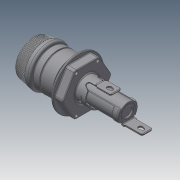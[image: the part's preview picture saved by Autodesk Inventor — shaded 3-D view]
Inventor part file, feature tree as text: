
AUTODESK INVENTOR PART (.ipt)
format: ipt  version: 2020.3 (Build 243373000, 373)  size: 3,708,928 bytes
history: native  units: in
note: dims shown in document units (in); Inventor stores cm internally (conversion verified against a paired STEP export)
features: fillet x2, revolve x1, other x1, pattern_circular x1
ambient origin geometry x8: Origin, YZ Plane, XZ Plane, XY Plane, X Axis, Y Axis, Z Axis, Center Point
bodies: Solid1 (feature_tree), Solid2 (feature_tree), Solid3 (feature_tree), Solid4 (feature_tree), Solid5 (feature_tree)
feature tree (5):
  fillet  "Fillet8"  [1 undecoded]
  revolve  "Revolve3"  [1 undecoded]
  other  "Cut-Extrude8"
  pattern_circular  "CirPattern1"
  fillet  "Fillet9"  [1 undecoded]
note: 3 required parameter values undecoded (feature->parameter linkage not recoverable at this tier; creation-order binding heuristic only, values carry confidence <= 0.55)
